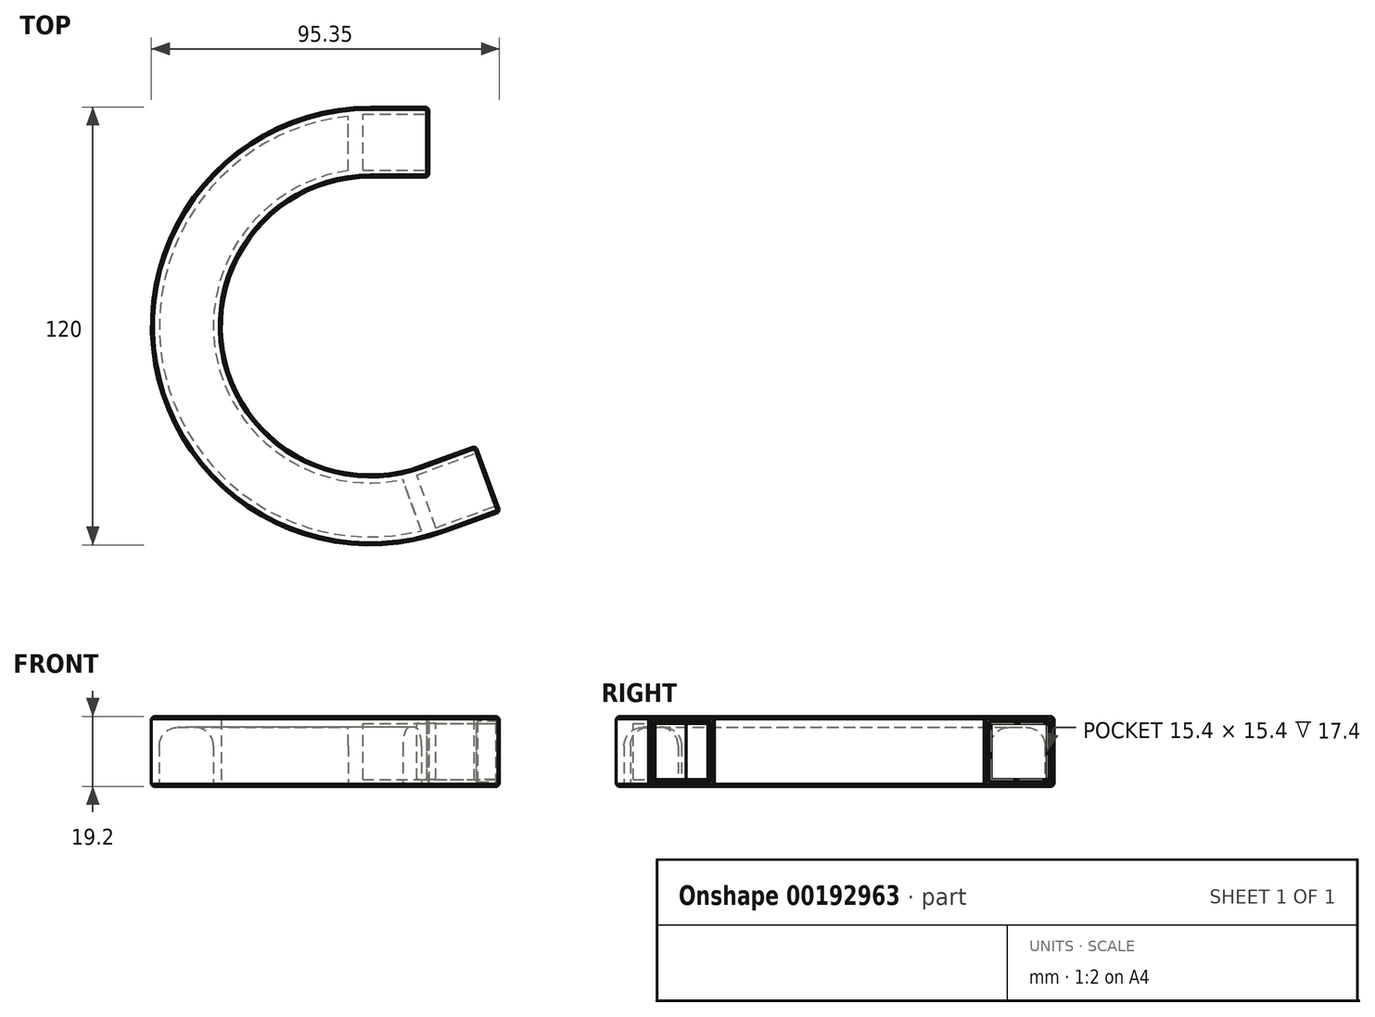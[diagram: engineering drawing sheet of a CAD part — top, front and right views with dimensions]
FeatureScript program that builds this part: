
annotation { "Feature Type Name" : "Feature", "Feature Type Description" : "" }
export const myFeature = defineFeature(function(context is Context, id is Id, definition is map)
    precondition{}
    {
        {
            var Q0;
            Q0=qCreatedBy(makeId("Top.planeOp"),FACE);
            var sketch = newSketch(context, id + "F0", { "sketchPlane" : qUnion([Q0])});
            skCircle(sketch, "E0", {"center": v(0, 0) * mm, "radius": 60 * mm});
            skCircle(sketch, "E1", {"center": v(0, 0) * mm, "radius": 40.8 * mm});
            skLineSegment(sketch, "E2", {"start": v(0, 0) * mm, "end": v(0, 60) * mm});
            skLineSegment(sketch, "E3", {"start": v(0, 0) * mm, "end": v(20.52, -56.38) * mm});
            skSolve(sketch);
        }
        {
            var Q0;
            {var subQ0=sQuery(id+"F0.wireOp",EDGE,"E2");var subQ1=sQuery(id+"F0.wireOp",EDGE,"E0");var subQ2=makeQuery(id+"F0.imprint","INTERSECT",VERTEX,{"derivedFrom":[subQ1,subQ0]});Q0=makeQuery(id+"F0.imprint","IMPRINT",FACE,{"disambiguationData":[TD([[makeQuery(id+"F0.imprint","IMPRINT",EDGE,{"disambiguationData":[TD([[subQ2,-1.0]])],"derivedFrom":subQ1}),1.0]])]});}
            extrude(context, id + "F1", {"entities" : qUnion([Q0]), "depth" : 19.2 * mm});
        }
        {
            var Q0;
            Q0=makeQuery(id+"F1.opExtrude","SWEPT_FACE",FACE,{"disambiguationData":[OSD([sQuery(id+"F0.wireOp",EDGE,"E2")])]});
            extrude(context, id + "F2", {"entities" : qUnion([Q0]), "operationType" : NewBodyOperationType.ADD, "depth" : 16 * mm});
        }
        {
            var Q0;
            Q0=makeQuery(id+"F1.opExtrude","SWEPT_FACE",FACE,{"disambiguationData":[OSD([sQuery(id+"F0.wireOp",EDGE,"E3")])]});
            extrude(context, id + "F3", {"entities" : qUnion([Q0]), "operationType" : NewBodyOperationType.ADD, "depth" : 16 * mm});
        }
        {
            var Q0;
            Q0=makeQuery(id+"F2.opExtrude","CAP_FACE",FACE,{"disambiguationData":[OSD([sQuery(id+"F0.wireOp",EDGE,"E2")])],"isStart":false});
            var sketch = newSketch(context, id + "F4", { "sketchPlane" : qUnion([Q0])});
            skLineSegment(sketch, "E4.bottom", {"start": v(42.7, 1.9) * mm, "end": v(58.1, 1.9) * mm});
            skLineSegment(sketch, "E4.top", {"start": v(42.7, 17.3) * mm, "end": v(58.1, 17.3) * mm});
            skLineSegment(sketch, "E4.left", {"start": v(42.7, 1.9) * mm, "end": v(42.7, 17.3) * mm});
            skLineSegment(sketch, "E4.right", {"start": v(58.1, 1.9) * mm, "end": v(58.1, 17.3) * mm});
            skPoint(sketch, "E4.middle", {"position": v(50.4, 9.6) * mm});
            skPoint(sketch, "E4.middle.positionSnap0", {"position": v(50.4, 19.2) * mm});
            skPoint(sketch, "E4.middle.positionSnap1", {"position": v(60, 9.6) * mm});
            skPoint(sketch, "E4.centerSnap0", {"position": v(50.4, 19.2) * mm});
            skPoint(sketch, "E4.centerSnap1", {"position": v(60, 9.6) * mm});
            skSolve(sketch);
        }
        {
            var Q0;
            Q0 = qSketchRegion(id + "F4", true);
            extrude(context, id + "F5", {"entities" : qUnion([Q0]), "operationType" : NewBodyOperationType.REMOVE, "oppositeDirection" : true, "depth" : 18 * mm});
        }
        {
            var Q0;
            Q0=makeQuery(id+"F3.opExtrude","CAP_FACE",FACE,{"disambiguationData":[OSD([sQuery(id+"F0.wireOp",EDGE,"E3")])],"isStart":false});
            var sketch = newSketch(context, id + "F6", { "sketchPlane" : qUnion([Q0])});
            skLineSegment(sketch, "E5.bottom", {"start": v(-58.1, 1.9) * mm, "end": v(-42.7, 1.9) * mm});
            skLineSegment(sketch, "E5.top", {"start": v(-58.1, 17.3) * mm, "end": v(-42.7, 17.3) * mm});
            skLineSegment(sketch, "E5.left", {"start": v(-58.1, 1.9) * mm, "end": v(-58.1, 17.3) * mm});
            skLineSegment(sketch, "E5.right", {"start": v(-42.7, 1.9) * mm, "end": v(-42.7, 17.3) * mm});
            skPoint(sketch, "E5.middle", {"position": v(-50.4, 9.6) * mm});
            skPoint(sketch, "E5.middle.positionSnap0", {"position": v(-50.4, 19.2) * mm});
            skPoint(sketch, "E5.middle.positionSnap1", {"position": v(-40.8, 9.6) * mm});
            skPoint(sketch, "E5.centerSnap0", {"position": v(-50.4, 19.2) * mm});
            skPoint(sketch, "E5.centerSnap1", {"position": v(-40.8, 9.6) * mm});
            skSolve(sketch);
        }
        {
            var Q0;
            Q0 = qSketchRegion(id + "F6", true);
            extrude(context, id + "F7", {"entities" : qUnion([Q0]), "operationType" : NewBodyOperationType.REMOVE, "oppositeDirection" : true, "depth" : 18 * mm});
        }
        {
            var Q0;
            Q0=makeQuery(id+"F1.opExtrude","CAP_EDGE",EDGE,{"disambiguationData":[OSD([sQuery(id+"F0.wireOp",EDGE,"E1")])],"isStart":false});
            var Q1;
            Q1=makeQuery(id+"F1.opExtrude","CAP_EDGE",EDGE,{"disambiguationData":[OSD([sQuery(id+"F0.wireOp",EDGE,"E0")])],"isStart":false});
            var Q2;
            Q2=makeQuery(id+"F1.opExtrude","CAP_EDGE",EDGE,{"disambiguationData":[OSD([sQuery(id+"F0.wireOp",EDGE,"E1")])],"isStart":true});
            var Q3;
            Q3=makeQuery(id+"F1.opExtrude","CAP_EDGE",EDGE,{"disambiguationData":[OSD([sQuery(id+"F0.wireOp",EDGE,"E0")])],"isStart":true});
            var Q4;
            Q4=makeQuery(id+"F2.opExtrude","CAP_FACE",FACE,{"disambiguationData":[OSD([sQuery(id+"F0.wireOp",EDGE,"E2")])],"isStart":false});
            var Q5;
            Q5=makeQuery(id+"F3.opExtrude","CAP_FACE",FACE,{"disambiguationData":[OSD([sQuery(id+"F0.wireOp",EDGE,"E3")])],"isStart":false});
            chamfer(context, id + "F8", {"entities" : qUnion([Q0, Q1, Q2, Q3, Q4, Q5]), "width" : 0.6 * mm, "tangentPropagation" : true});
        }
        {
            var Q0;
            {var subQ0=sQuery(id+"F0.wireOp",EDGE,"E3");var subQ1=sQuery(id+"F0.wireOp",EDGE,"E2");Q0=makeQuery(id+"F3.boolean.opBoolean","MERGE",FACE,{"derivedFrom":[makeQuery(id+"F2.boolean.opBoolean","MERGE",FACE,{"derivedFrom":[makeQuery(id+"F1.opExtrude","CAP_FACE",FACE,{"disambiguationData":[OSD([sQuery(id+"F0.wireOp",EDGE,"E0"),sQuery(id+"F0.wireOp",EDGE,"E1"),subQ1,subQ0])],"isStart":true}),makeQuery(id+"F2.opExtrude","SWEPT_FACE",FACE,{"disambiguationData":[OSD([subQ1]),TDD([makeQuery(id+"F1.opExtrude","CAP_EDGE",EDGE,{"disambiguationData":[OSD([subQ1])],"isStart":true})])]})]}),makeQuery(id+"F3.opExtrude","SWEPT_FACE",FACE,{"disambiguationData":[OSD([subQ0]),TDD([makeQuery(id+"F1.opExtrude","CAP_EDGE",EDGE,{"disambiguationData":[OSD([subQ0])],"isStart":true})])]})]});}
            var sketch = newSketch(context, id + "F9", { "sketchPlane" : qUnion([Q0])});
            skLineSegment(sketch, "E6.0", {"start": v(17.23, 64.9) * mm, "end": v(5.54, 32.75) * mm});
            skLineSegment(sketch, "E7.0", {"start": v(-6, -34.96) * mm, "end": v(-6, -67.06) * mm});
            skArc(sketch, "E8.0", {"start": v(19.77, 54.31) * mm, "mid": v(-56.92, 10.04) * mm, "end": v(0, -57.8) * mm});
            skArc(sketch, "E9.0", {"start": v(0, -43) * mm, "mid": v(-42.35, 7.47) * mm, "end": v(14.7, 40.4) * mm});
            skSolve(sketch);
        }
        {
            var Q0;
            Q0 = qSketchRegion(id + "F9", true);
            extrude(context, id + "F10", {"entities" : qUnion([Q0]), "operationType" : NewBodyOperationType.REMOVE, "oppositeDirection" : true, "depth" : 16.2 * mm});
        }
        {
            var Q0;
            Q0=makeQuery(id+"F10.boolean.opBoolean","COPY",EDGE,{"derivedFrom":makeQuery(id+"F10.opExtrude","CAP_EDGE",EDGE,{"disambiguationData":[OSD([sQuery(id+"F9.wireOp",EDGE,"E8.0")])],"isStart":false})});
            var Q1;
            Q1=makeQuery(id+"F10.boolean.opBoolean","COPY",EDGE,{"derivedFrom":makeQuery(id+"F10.opExtrude","CAP_EDGE",EDGE,{"disambiguationData":[OSD([sQuery(id+"F9.wireOp",EDGE,"E9.0")])],"isStart":false})});
            fillet(context, id + "F11", {"entities" : qUnion([Q0, Q1]), "radius" : 5 * mm, "tangentPropagation" : true, "allowEdgeOverflow" : false});
        }
    });
